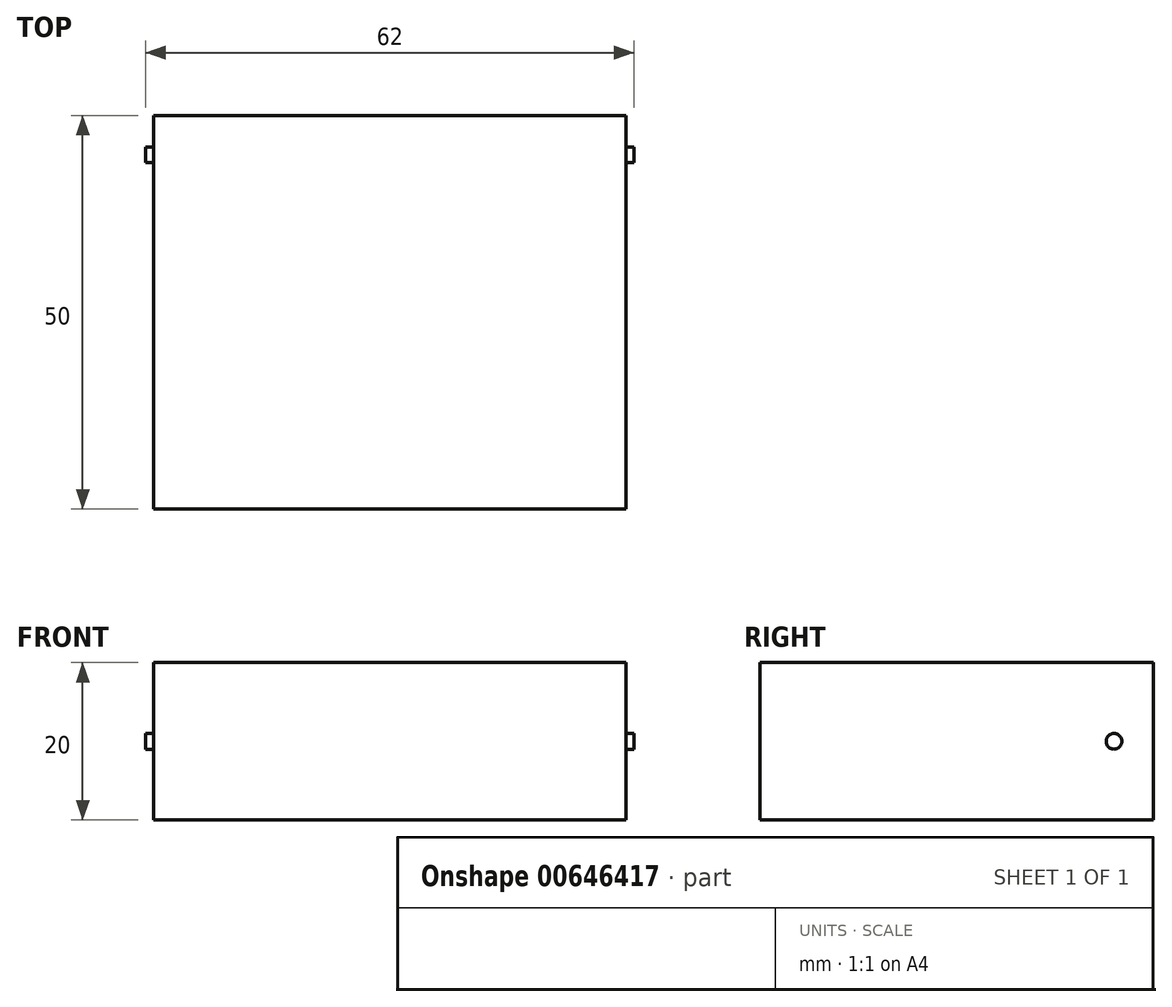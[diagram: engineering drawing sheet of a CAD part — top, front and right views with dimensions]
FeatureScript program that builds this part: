
annotation { "Feature Type Name" : "Feature", "Feature Type Description" : "" }
export const myFeature = defineFeature(function(context is Context, id is Id, definition is map)
    precondition{}
    {
        {
            var Q0;
            Q0=qCreatedBy(makeId("Top.planeOp"),FACE);
            var sketch = newSketch(context, id + "F0", { "sketchPlane" : qUnion([Q0])});
            skLineSegment(sketch, "E0.bottom", {"start": v(0, 0) * mm, "end": v(60, 0) * mm});
            skLineSegment(sketch, "E0.top", {"start": v(0, -50) * mm, "end": v(60, -50) * mm});
            skLineSegment(sketch, "E0.left", {"start": v(0, 0) * mm, "end": v(0, -50) * mm});
            skLineSegment(sketch, "E0.right", {"start": v(60, 0) * mm, "end": v(60, -50) * mm});
            skSolve(sketch);
        }
        {
            var Q0;
            Q0=makeQuery(id+"F0.imprint","IMPRINT",FACE,{"disambiguationData":[TD([[makeQuery(id+"F0.imprint","IMPRINT",EDGE,{"derivedFrom":sQuery(id+"F0.wireOp",EDGE,"E0.bottom")}),-1.0]])]});
            extrude(context, id + "F1", {"entities" : qUnion([Q0]), "depth" : 20 * mm, "offsetDistance" : 25 * mm});
        }
        {
            var Q0;
            Q0=makeQuery(id+"F1.opExtrude","SWEPT_FACE",FACE,{"disambiguationData":[OSD([sQuery(id+"F0.wireOp",EDGE,"E0.right")])]});
            var sketch = newSketch(context, id + "F2", { "sketchPlane" : qUnion([Q0])});
            skLineSegment(sketch, "E1", {"start": v(0, 10) * mm, "end": v(-5, 10) * mm, "construction": true});
            skCircle(sketch, "E2", {"center": v(-5, 10) * mm, "radius": 1 * mm});
            skSolve(sketch);
        }
        {
            var Q0;
            Q0 = qSketchRegion(id + "F2", true);
            extrude(context, id + "F3", {"entities" : qUnion([Q0]), "operationType" : NewBodyOperationType.ADD, "depth" : 1 * mm, "offsetDistance" : 25 * mm});
        }
        {
            var Q0;
            Q0=makeQuery(id+"F3.opExtrude","CAP_FACE",FACE,{"disambiguationData":[OSD([sQuery(id+"F2.wireOp",EDGE,"E2")])],"isStart":false});
            extrude(context, id + "F4", {"entities" : qUnion([Q0]), "operationType" : NewBodyOperationType.ADD, "oppositeDirection" : true, "depth" : 62 * mm, "offsetDistance" : 25 * mm});
        }
    });
